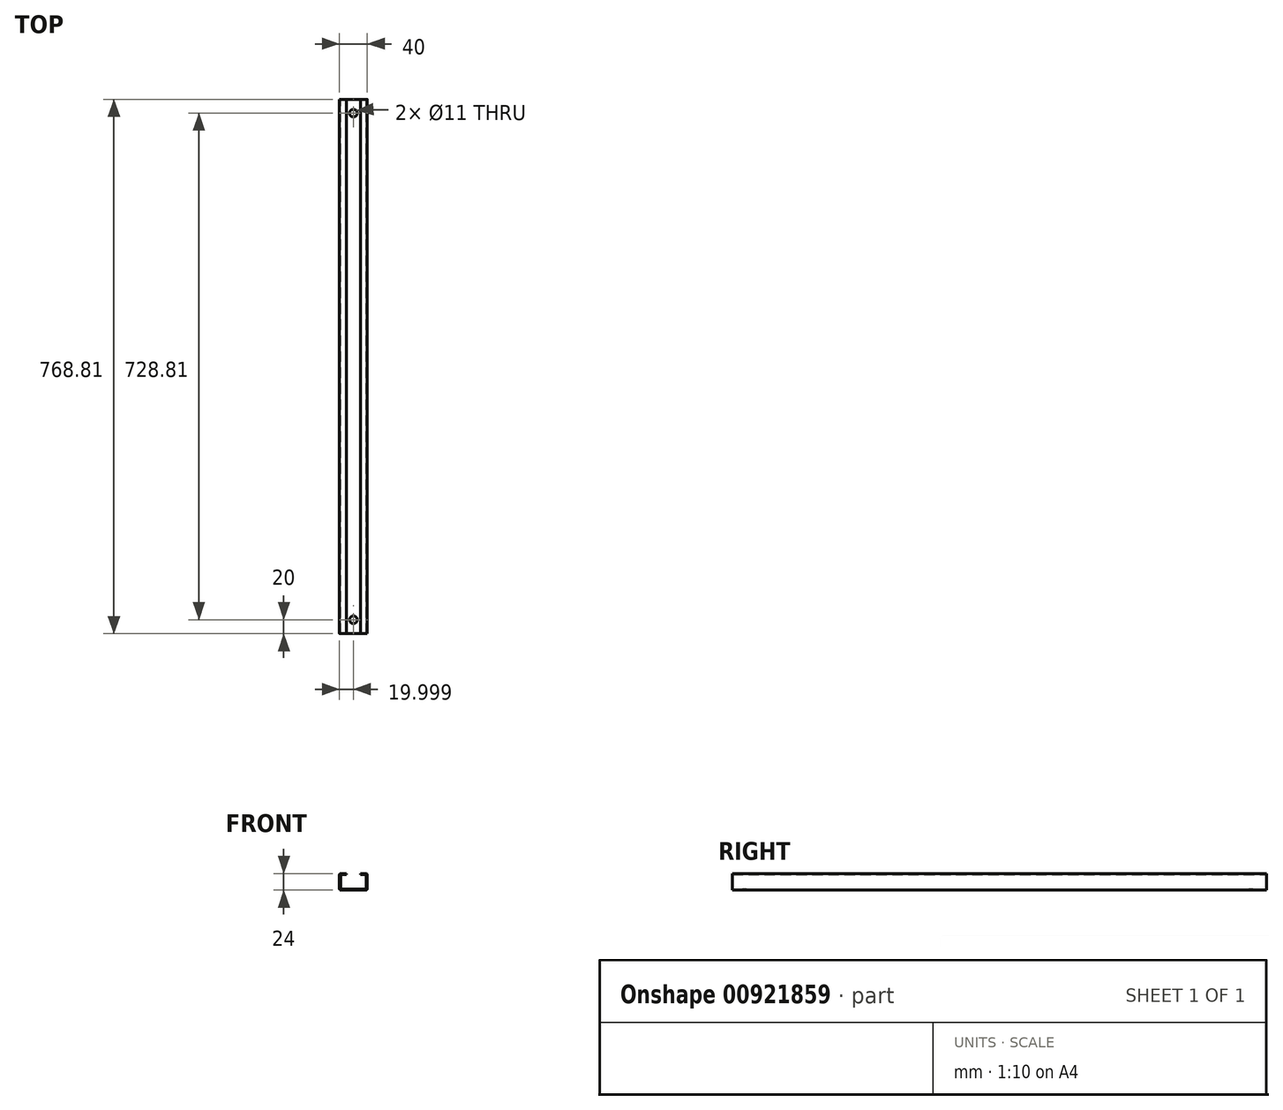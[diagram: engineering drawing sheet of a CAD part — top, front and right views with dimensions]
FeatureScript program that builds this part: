
annotation { "Feature Type Name" : "Feature", "Feature Type Description" : "" }
export const myFeature = defineFeature(function(context is Context, id is Id, definition is map)
    precondition{}
    {
        {
            var Q0;
            Q0=qCreatedBy(makeId("Front.planeOp"),FACE);
            var sketch = newSketch(context, id + "F0", { "sketchPlane" : qUnion([Q0])});
            skLineSegment(sketch, "E0.top", {"start": v(-81.45, 32.5) * mm, "end": v(-45.45, 32.5) * mm});
            skLineSegment(sketch, "E0.left", {"start": v(-83.45, 54.5) * mm, "end": v(-83.45, 34.5) * mm});
            skLineSegment(sketch, "E0.right", {"start": v(-43.45, 54.5) * mm, "end": v(-43.45, 34.5) * mm});
            skLineSegment(sketch, "E1.1", {"start": v(-81.95, 54) * mm, "end": v(-81.95, 35) * mm});
            skLineSegment(sketch, "E1.2", {"start": v(-80.95, 34) * mm, "end": v(-45.95, 34) * mm});
            skLineSegment(sketch, "E1.3", {"start": v(-44.95, 54) * mm, "end": v(-44.95, 35) * mm});
            skLineSegment(sketch, "E2", {"start": v(-45.45, 56.5) * mm, "end": v(-53.45, 56.5) * mm});
            skLineSegment(sketch, "E3", {"start": v(-53.45, 56.5) * mm, "end": v(-53.45, 55) * mm});
            skLineSegment(sketch, "E4", {"start": v(-53.45, 55) * mm, "end": v(-45.95, 55) * mm});
            skLineSegment(sketch, "E5", {"start": v(-81.45, 56.5) * mm, "end": v(-73.45, 56.5) * mm});
            skLineSegment(sketch, "E6", {"start": v(-73.45, 56.5) * mm, "end": v(-73.45, 55) * mm});
            skLineSegment(sketch, "E7", {"start": v(-73.45, 55) * mm, "end": v(-80.95, 55) * mm});
            skPoint(sketch, "E8.visualSharp", {"position": v(-83.45, 56.5) * mm});
            skArc(sketch, "E8.filletArc", {"start": v(-81.45, 56.5) * mm, "mid": v(-82.87, 55.92) * mm, "end": v(-83.45, 54.5) * mm});
            skPoint(sketch, "E9.visualSharp", {"position": v(-83.45, 32.5) * mm});
            skArc(sketch, "E9.filletArc", {"start": v(-83.45, 34.5) * mm, "mid": v(-82.87, 33.09) * mm, "end": v(-81.45, 32.5) * mm});
            skPoint(sketch, "E10.visualSharp", {"position": v(-43.45, 32.5) * mm});
            skArc(sketch, "E10.filletArc", {"start": v(-45.45, 32.5) * mm, "mid": v(-44.04, 33.09) * mm, "end": v(-43.45, 34.5) * mm});
            skPoint(sketch, "E11.visualSharp", {"position": v(-43.45, 56.5) * mm});
            skArc(sketch, "E11.filletArc", {"start": v(-43.45, 54.5) * mm, "mid": v(-44.04, 55.92) * mm, "end": v(-45.45, 56.5) * mm});
            skPoint(sketch, "E12.visualSharp", {"position": v(-44.95, 55) * mm});
            skArc(sketch, "E12.filletArc", {"start": v(-44.95, 54) * mm, "mid": v(-45.24, 54.7) * mm, "end": v(-45.95, 55) * mm});
            skPoint(sketch, "E13.visualSharp", {"position": v(-44.95, 34) * mm});
            skArc(sketch, "E13.filletArc", {"start": v(-45.95, 34) * mm, "mid": v(-45.24, 34.3) * mm, "end": v(-44.95, 35) * mm});
            skPoint(sketch, "E14.visualSharp", {"position": v(-81.95, 34) * mm});
            skArc(sketch, "E14.filletArc", {"start": v(-81.95, 35) * mm, "mid": v(-81.66, 34.3) * mm, "end": v(-80.95, 34) * mm});
            skPoint(sketch, "E15.visualSharp", {"position": v(-81.95, 55) * mm});
            skArc(sketch, "E15.filletArc", {"start": v(-80.95, 55) * mm, "mid": v(-81.66, 54.7) * mm, "end": v(-81.95, 54) * mm});
            skSolve(sketch);
        }
        {
            var Q0;
            Q0=makeQuery(id+"F0.imprint","IMPRINT",FACE,{"disambiguationData":[TD([[makeQuery(id+"F0.imprint","IMPRINT",EDGE,{"derivedFrom":sQuery(id+"F0.wireOp",EDGE,"E0.top")}),1.0]])]});
            extrude(context, id + "F1", {"entities" : qUnion([Q0]), "depth" : 768.8 * mm, "offsetDistance" : 25 * mm});
        }
        {
            var Q0;
            Q0=makeQuery(id+"F1.opExtrude","SWEPT_FACE",FACE,{"disambiguationData":[OSD([sQuery(id+"F0.wireOp",EDGE,"E0.top")])]});
            var sketch = newSketch(context, id + "F2", { "sketchPlane" : qUnion([Q0])});
            skCircle(sketch, "E16", {"center": v(-63.45, 748.8) * mm, "radius": 4.31 * mm});
            skCircle(sketch, "E17", {"center": v(-63.45, 20) * mm, "radius": 4.31 * mm});
            skSolve(sketch);
        }
        {
            var Q0;
            Q0=sQuery(id+"F2.wireOp",VERTEX,"E16.center");
            var Q1;
            Q1=sQuery(id+"F2.wireOp",VERTEX,"E17.center");
            var Q2;
            Q2=makeQuery(id+"F1.opExtrude","SWEPT_BODY",BODY,{"disambiguationData":[OSD([sQuery(id+"F0.wireOp",EDGE,"E0.top"),sQuery(id+"F0.wireOp",EDGE,"E0.left"),sQuery(id+"F0.wireOp",EDGE,"E0.right"),sQuery(id+"F0.wireOp",EDGE,"E1.1"),sQuery(id+"F0.wireOp",EDGE,"E1.2"),sQuery(id+"F0.wireOp",EDGE,"E1.3"),sQuery(id+"F0.wireOp",EDGE,"E2"),sQuery(id+"F0.wireOp",EDGE,"E3"),sQuery(id+"F0.wireOp",EDGE,"E4"),sQuery(id+"F0.wireOp",EDGE,"E5"),sQuery(id+"F0.wireOp",EDGE,"E6"),sQuery(id+"F0.wireOp",EDGE,"E7"),sQuery(id+"F0.wireOp",EDGE,"E8.filletArc"),sQuery(id+"F0.wireOp",EDGE,"E9.filletArc"),sQuery(id+"F0.wireOp",EDGE,"E10.filletArc"),sQuery(id+"F0.wireOp",EDGE,"E11.filletArc"),sQuery(id+"F0.wireOp",EDGE,"E12.filletArc"),sQuery(id+"F0.wireOp",EDGE,"E13.filletArc"),sQuery(id+"F0.wireOp",EDGE,"E14.filletArc"),sQuery(id+"F0.wireOp",EDGE,"E15.filletArc")])]});
            hole(context, id + "F3", {"style" : HoleStyle.SIMPLE, "endStyle" : HoleEndStyle.THROUGH, "holeDiameter" : 11 * mm, "majorDiameter" : 5 * mm, "isTappedThrough" : true, "tappedDepth" : 12 * mm, "tapClearance" : 3, "locations" : qUnion([Q0, Q1]), "scope" : qUnion([Q2])});
        }
    });
